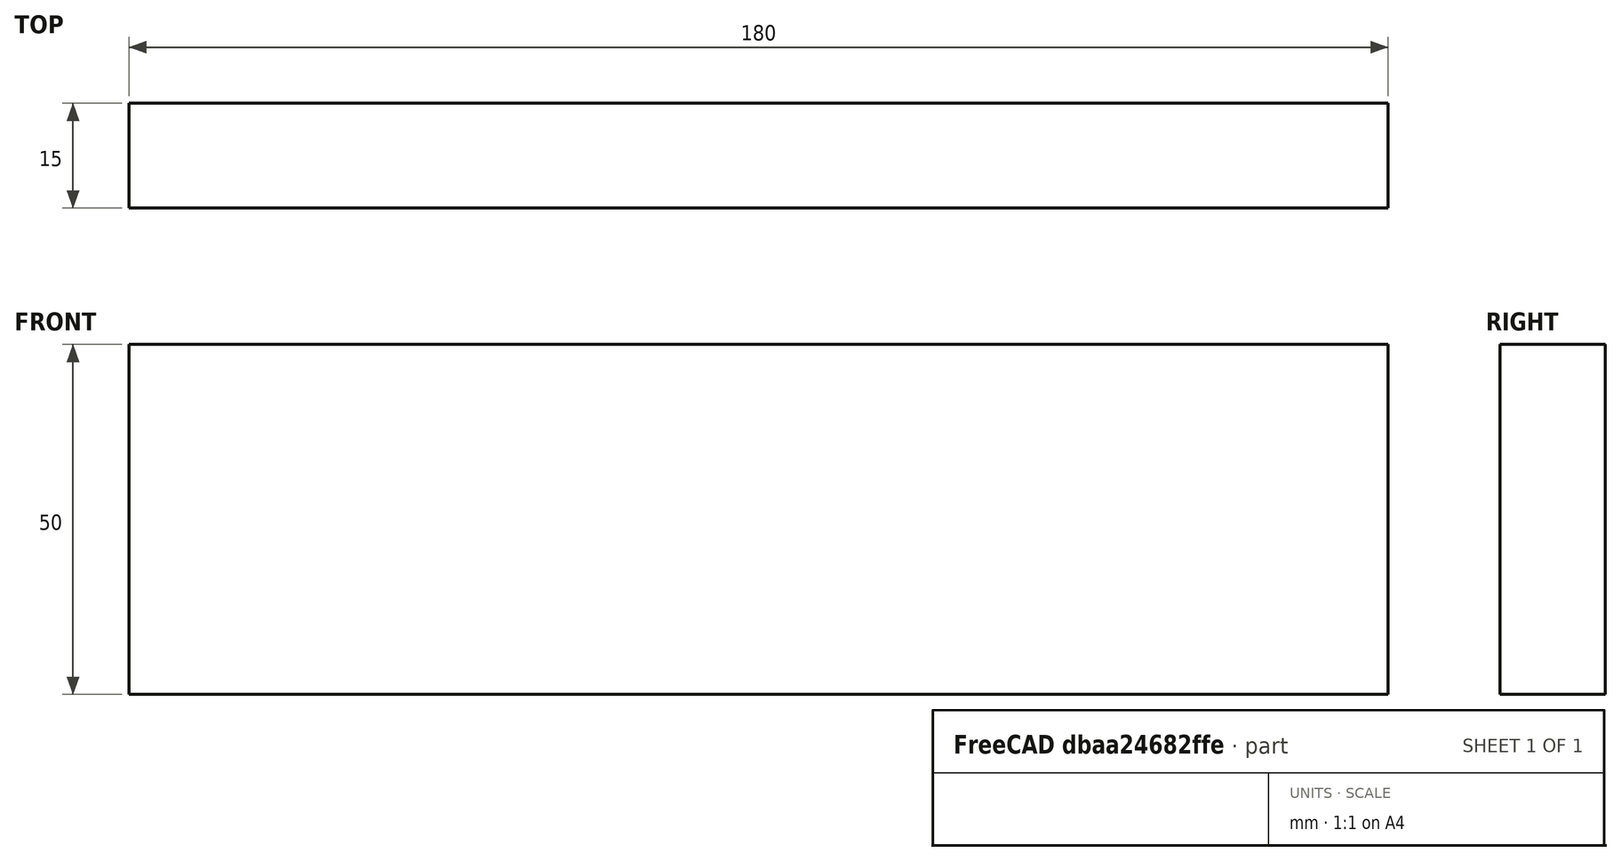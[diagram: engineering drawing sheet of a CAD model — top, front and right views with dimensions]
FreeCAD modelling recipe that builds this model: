
FCSTD DOCUMENT  (FreeCAD 0.15R4671 (Git))
Label: Flat Bar 180x15 EN10058 S235JR
License: All rights reserved
LicenseURL: http://en.wikipedia.org/wiki/All_rights_reserved
objects: Sketcher::SketchObject×1, Part::Extrusion×1
note: 2 computed .brp shape members not serialized (recipe doc carries the construction recipe); baked Part::Feature solids carry a one-line shape summary decoded from their .brp

FEATURE [Sketcher::SketchObject] Sketch
  sketch-geometry (4):
    g0: LineSegment StartX=-90 StartY=-7.5 StartZ=0 EndX=90 EndY=-7.5 EndZ=0
    g1: LineSegment StartX=90 StartY=-7.5 StartZ=0 EndX=90 EndY=7.5 EndZ=0
    g2: LineSegment StartX=90 StartY=7.5 StartZ=0 EndX=-90 EndY=7.5 EndZ=0
    g3: LineSegment StartX=-90 StartY=7.5 StartZ=0 EndX=-90 EndY=-7.5 EndZ=0
  constraints (12):
    c: Coincident(g0,g1)
    c: Coincident(g1,g2)
    c: Coincident(g2,g3)
    c: Coincident(g3,g0)
    c: Horizontal(g0)
    c: Horizontal(g2)
    c: Vertical(g1)
    c: Vertical(g3)
    c: Symmetric(g1,g2,g-2)
    c: Symmetric(g0,g1,g-1)
    c: DistanceY(g1) = 15
    c: DistanceX(g0) = 180
FEATURE [Part::Extrusion] Extrude  label="Flat Bar 180x15 EN10058 S235JR"
  Base = -> Sketch
  Dir = (0,0,50)
  Solid = true
